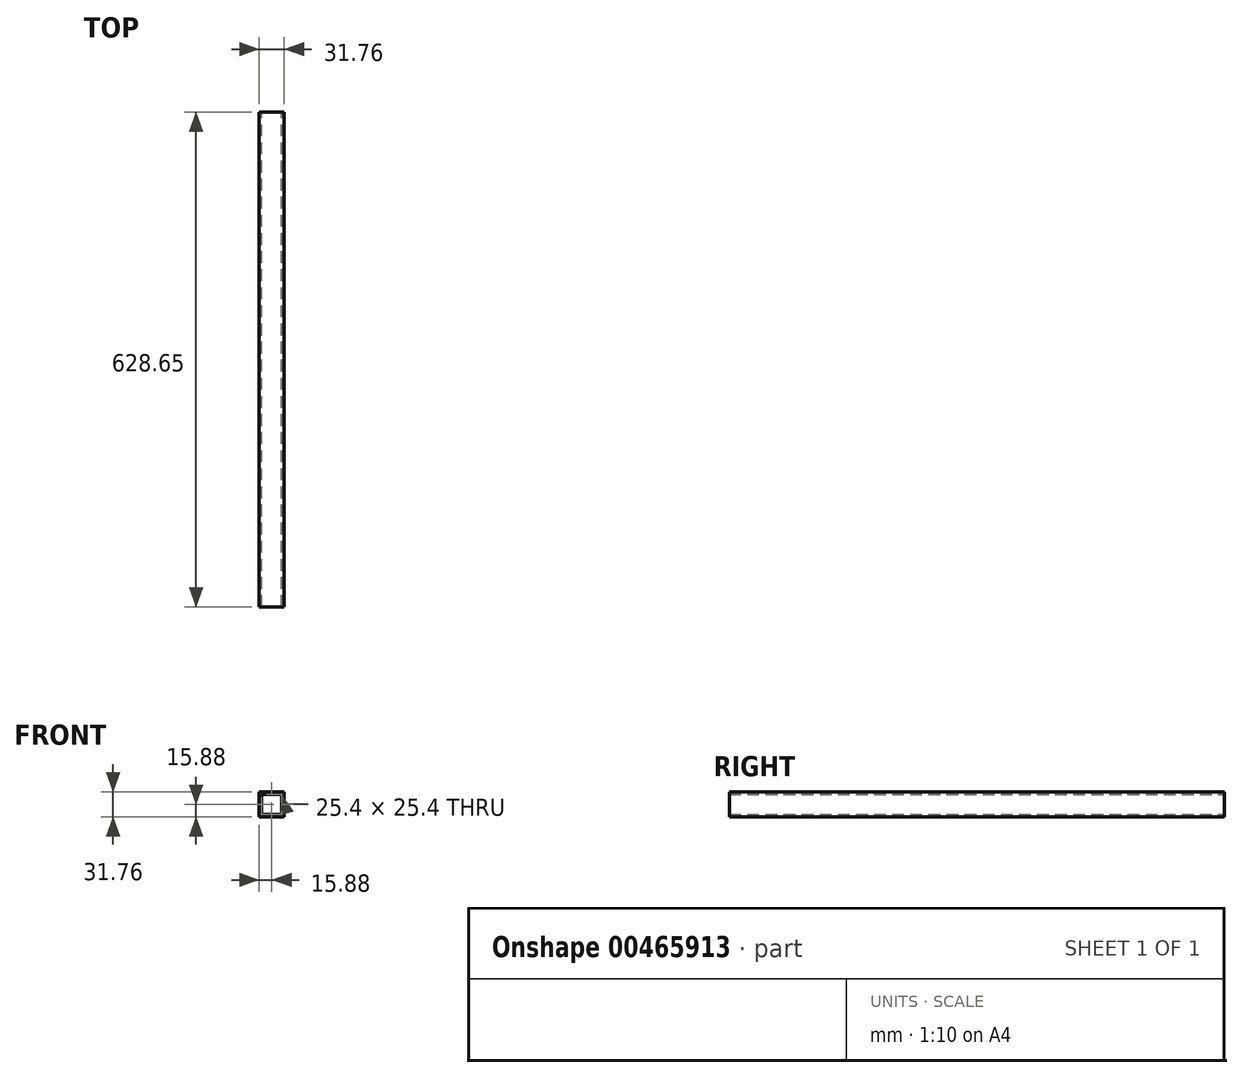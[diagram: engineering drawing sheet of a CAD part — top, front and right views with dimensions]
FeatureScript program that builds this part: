
annotation { "Feature Type Name" : "Feature", "Feature Type Description" : "" }
export const myFeature = defineFeature(function(context is Context, id is Id, definition is map)
    precondition{}
    {
        {
            var Q0;
            Q0=qCreatedBy(makeId("Front.planeOp"),FACE);
            var sketch = newSketch(context, id + "F0", { "sketchPlane" : qUnion([Q0])});
            skLineSegment(sketch, "E0.bottom", {"start": v(-15.87, 15.88) * mm, "end": v(15.88, 15.88) * mm});
            skLineSegment(sketch, "E0.top", {"start": v(-15.88, -15.88) * mm, "end": v(15.87, -15.88) * mm});
            skLineSegment(sketch, "E0.left", {"start": v(-15.87, 15.88) * mm, "end": v(-15.88, -15.88) * mm});
            skLineSegment(sketch, "E0.right", {"start": v(15.88, 15.88) * mm, "end": v(15.87, -15.88) * mm});
            skPoint(sketch, "E0.middle", {"position": v(0, 0) * mm});
            skLineSegment(sketch, "E1.bottom", {"start": v(-12.7, 12.7) * mm, "end": v(12.7, 12.7) * mm});
            skLineSegment(sketch, "E1.top", {"start": v(-12.7, -12.7) * mm, "end": v(12.7, -12.7) * mm});
            skLineSegment(sketch, "E1.left", {"start": v(-12.7, 12.7) * mm, "end": v(-12.7, -12.7) * mm});
            skLineSegment(sketch, "E1.right", {"start": v(12.7, 12.7) * mm, "end": v(12.7, -12.7) * mm});
            skSolve(sketch);
        }
        {
            var Q0;
            Q0=makeQuery(id+"F0.imprint","IMPRINT",FACE,{"disambiguationData":[TD([[makeQuery(id+"F0.imprint","IMPRINT",EDGE,{"derivedFrom":sQuery(id+"F0.wireOp",EDGE,"E0.bottom")}),-1.0]])]});
            extrude(context, id + "F1", {"entities" : qUnion([Q0]), "depth" : 628.65 * mm});
        }
    });
